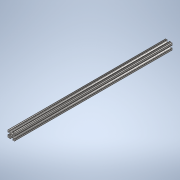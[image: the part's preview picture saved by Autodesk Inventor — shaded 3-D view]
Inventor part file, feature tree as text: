
AUTODESK INVENTOR PART (.ipt)
format: ipt  version: 2020 (Build 240168000, 168)  size: 240,640 bytes
history: native  units: in
note: dims shown in document units (in); Inventor stores cm internally (conversion verified against a paired STEP export)
features: extrude x1, sketch x1
ambient origin geometry x8: Origin, YZ Plane, XZ Plane, XY Plane, X Axis, Y Axis, Z Axis, Center Point
bodies: Solid1 (feature_tree)
feature tree (2):
  extrude  "Extrusion1"  [1 undecoded]
  sketch  "Sketch1"  dims[d0=22.0in d1=0.0in]
note: 1 required parameter value undecoded (feature->parameter linkage not recoverable at this tier; creation-order binding heuristic only, values carry confidence <= 0.55)
